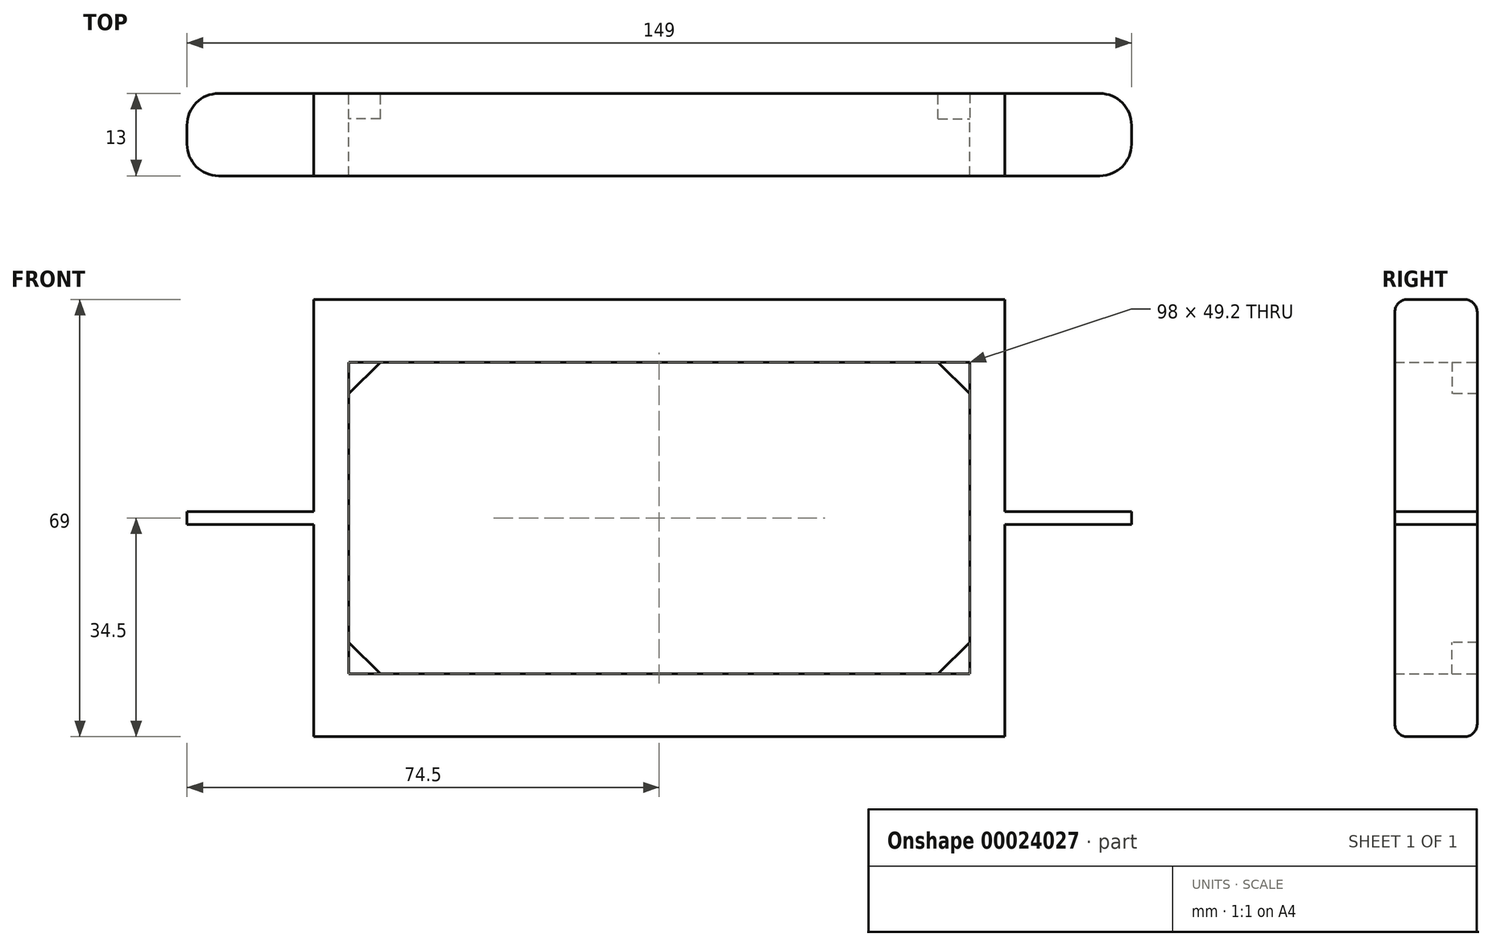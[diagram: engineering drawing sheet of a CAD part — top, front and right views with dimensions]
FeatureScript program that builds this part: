
annotation { "Feature Type Name" : "Feature", "Feature Type Description" : "" }
export const myFeature = defineFeature(function(context is Context, id is Id, definition is map)
    precondition{}
    {
        {
            var Q0;
            Q0=qCreatedBy(makeId("Front.planeOp"),FACE);
            var sketch = newSketch(context, id + "F0", { "sketchPlane" : qUnion([Q0])});
            skLineSegment(sketch, "E0.bottom", {"start": v(-49, -24.6) * mm, "end": v(49, -24.6) * mm});
            skLineSegment(sketch, "E0.top", {"start": v(-49, 24.6) * mm, "end": v(49, 24.6) * mm});
            skLineSegment(sketch, "E0.left", {"start": v(-49, -24.6) * mm, "end": v(-49, 24.6) * mm});
            skLineSegment(sketch, "E0.right", {"start": v(49, -24.6) * mm, "end": v(49, 24.6) * mm});
            skPoint(sketch, "E0.middle", {"position": v(0, 0) * mm});
            skLineSegment(sketch, "E1.bottom", {"start": v(54.5, -34.5) * mm, "end": v(-54.5, -34.5) * mm});
            skLineSegment(sketch, "E1.top", {"start": v(54.5, 34.5) * mm, "end": v(-54.5, 34.5) * mm});
            skLineSegment(sketch, "E1.left", {"start": v(54.5, -34.5) * mm, "end": v(54.5, 34.5) * mm});
            skLineSegment(sketch, "E1.right", {"start": v(-54.5, -34.5) * mm, "end": v(-54.5, 34.5) * mm});
            skLineSegment(sketch, "E2", {"start": v(0, 0) * mm, "end": v(0, -47.06) * mm, "construction": true});
            skLineSegment(sketch, "E3", {"start": v(54.5, 0) * mm, "end": v(74.5, 0) * mm, "construction": true});
            skPoint(sketch, "E3.endSnap0", {"position": v(54.5, 0) * mm});
            skLineSegment(sketch, "E4", {"start": v(74.5, 1) * mm, "end": v(74.5, -1) * mm});
            skLineSegment(sketch, "E5", {"start": v(74.5, -1) * mm, "end": v(54.5, -1) * mm});
            skLineSegment(sketch, "E6", {"start": v(74.5, 1) * mm, "end": v(54.5, 1) * mm});
            skLineSegment(sketch, "E7.MirrorCS", {"start": v(-74.5, -1) * mm, "end": v(-54.5, -1) * mm});
            skLineSegment(sketch, "E8.MirrorCS", {"start": v(-74.5, 1) * mm, "end": v(-54.5, 1) * mm});
            skLineSegment(sketch, "E9.MirrorCS", {"start": v(-74.5, 1) * mm, "end": v(-74.5, -1) * mm});
            skSolve(sketch);
        }
        {
            var Q0;
            Q0=makeQuery(id+"F0.imprint","IMPRINT",FACE,{"disambiguationData":[TD([[makeQuery(id+"F0.imprint","IMPRINT",EDGE,{"derivedFrom":sQuery(id+"F0.wireOp",EDGE,"E0.bottom")}),-1.0]])]});
            var Q1;
            Q1=makeQuery(id+"F0.imprint","IMPRINT",FACE,{"disambiguationData":[TD([[makeQuery(id+"F0.imprint","IMPRINT",EDGE,{"derivedFrom":sQuery(id+"F0.wireOp",EDGE,"E4")}),-1.0]])]});
            var Q2;
            {var subQ0=sQuery(id+"F0.wireOp",EDGE,"E7.MirrorCS");Q2=makeQuery(id+"F0.imprint","IMPRINT",FACE,{"disambiguationData":[TD([[makeQuery(id+"F0.imprint","IMPRINT",EDGE,{"derivedFrom":subQ0}),1.0]])]});}
            extrude(context, id + "F1", {"entities" : qUnion([Q0, Q1, Q2]), "depth" : 13 * mm});
        }
        {
            var Q0;
            Q0=makeQuery(id+"F1.opExtrude","SWEPT_FACE",FACE,{"disambiguationData":[OSD([sQuery(id+"F0.wireOp",EDGE,"E0.left")])]});
            var sketch = newSketch(context, id + "F2", { "sketchPlane" : qUnion([Q0])});
            skLineSegment(sketch, "E10", {"start": v(-6.5, 24.6) * mm, "end": v(-6.5, -24.6) * mm, "construction": true});
            skLineSegment(sketch, "E11", {"start": v(-4, 24.6) * mm, "end": v(-4, 19.6) * mm});
            skLineSegment(sketch, "E12", {"start": v(-4, 19.6) * mm, "end": v(0, 19.6) * mm});
            skLineSegment(sketch, "E13", {"start": v(-6.5, 0) * mm, "end": v(0, 0) * mm, "construction": true});
            skLineSegment(sketch, "E14.MirrorCS", {"start": v(-4, -24.6) * mm, "end": v(-4, -19.6) * mm});
            skLineSegment(sketch, "E15.MirrorCS", {"start": v(-4, -19.6) * mm, "end": v(0, -19.6) * mm});
            skSolve(sketch);
        }
        {
            var Q0;
            Q0=makeQuery(id+"F1.opExtrude","SWEPT_FACE",FACE,{"disambiguationData":[OSD([sQuery(id+"F0.wireOp",EDGE,"E0.right")])]});
            var sketch = newSketch(context, id + "F3", { "sketchPlane" : qUnion([Q0])});
            skLineSegment(sketch, "E16", {"start": v(0, 0) * mm, "end": v(13, 0) * mm, "construction": true});
            skLineSegment(sketch, "E17", {"start": v(6.5, 24.6) * mm, "end": v(6.5, 0) * mm, "construction": true});
            skLineSegment(sketch, "E18.bottom", {"start": v(0, 24.6) * mm, "end": v(4, 24.6) * mm});
            skLineSegment(sketch, "E18.top", {"start": v(0, 19.6) * mm, "end": v(4, 19.6) * mm});
            skLineSegment(sketch, "E18.left", {"start": v(0, 24.6) * mm, "end": v(0, 19.6) * mm});
            skLineSegment(sketch, "E18.right", {"start": v(4, 24.6) * mm, "end": v(4, 19.6) * mm});
            skLineSegment(sketch, "E19.MirrorCS", {"start": v(0, -19.6) * mm, "end": v(4, -19.6) * mm});
            skLineSegment(sketch, "E20.MirrorCS", {"start": v(4, -24.6) * mm, "end": v(4, -19.6) * mm});
            skSolve(sketch);
        }
        {
            var Q0;
            Q0 = qSketchRegion(id + "F2", true);
            var Q1;
            {var subQ0=sQuery(id+"F2.wireOp",EDGE,"E14.MirrorCS");Q1=makeQuery(id+"F2.imprint","IMPRINT",FACE,{"disambiguationData":[TD([[makeQuery(id+"F2.imprint","IMPRINT",EDGE,{"derivedFrom":subQ0}),-1.0]])]});}
            var Q2;
            {var subQ0=sQuery(id+"F2.wireOp",EDGE,"E11");Q2=makeQuery(id+"F2.imprint","IMPRINT",FACE,{"disambiguationData":[TD([[makeQuery(id+"F2.imprint","IMPRINT",EDGE,{"derivedFrom":subQ0}),1.0]])]});}
            extrude(context, id + "F4", {"entities" : qUnion([Q0, Q1, Q2]), "operationType" : NewBodyOperationType.ADD, "depth" : 5 * mm});
        }
        {
            var Q0;
            Q0 = qSketchRegion(id + "F3", true);
            var Q1;
            {var subQ0=sQuery(id+"F3.wireOp",EDGE,"E19.MirrorCS");Q1=makeQuery(id+"F3.imprint","IMPRINT",FACE,{"disambiguationData":[TD([[makeQuery(id+"F3.imprint","IMPRINT",EDGE,{"derivedFrom":subQ0}),-1.0]])]});}
            extrude(context, id + "F5", {"entities" : qUnion([Q0, Q1]), "operationType" : NewBodyOperationType.ADD, "depth" : 5 * mm});
        }
        {
            var Q0;
            Q0=makeQuery(id+"F4.opExtrude","CAP_EDGE",EDGE,{"disambiguationData":[OSD([sQuery(id+"F2.wireOp",EDGE,"E12")])],"isStart":false});
            var Q1;
            Q1=makeQuery(id+"F4.opExtrude","CAP_EDGE",EDGE,{"disambiguationData":[OSD([sQuery(id+"F2.wireOp",EDGE,"E15.MirrorCS")])],"isStart":false});
            var Q2;
            Q2=makeQuery(id+"F5.opExtrude","CAP_EDGE",EDGE,{"disambiguationData":[OSD([sQuery(id+"F3.wireOp",EDGE,"E18.top")])],"isStart":false});
            var Q3;
            Q3=makeQuery(id+"F5.opExtrude","CAP_EDGE",EDGE,{"disambiguationData":[OSD([sQuery(id+"F3.wireOp",EDGE,"E19.MirrorCS")])],"isStart":false});
            chamfer(context, id + "F6", {"entities" : qUnion([Q0, Q1, Q2, Q3]), "width" : 5 * mm, "tangentPropagation" : true});
        }
        {
            var Q0;
            Q0=makeQuery(id+"F1.opExtrude","CAP_EDGE",EDGE,{"disambiguationData":[OSD([sQuery(id+"F0.wireOp",EDGE,"E4")])],"isStart":false});
            var Q1;
            Q1=makeQuery(id+"F1.opExtrude","CAP_EDGE",EDGE,{"disambiguationData":[OSD([sQuery(id+"F0.wireOp",EDGE,"E4")])],"isStart":true});
            var Q2;
            Q2=makeQuery(id+"F1.opExtrude","CAP_EDGE",EDGE,{"disambiguationData":[OSD([sQuery(id+"F0.wireOp",EDGE,"E9.MirrorCS")])],"isStart":true});
            var Q3;
            Q3=makeQuery(id+"F1.opExtrude","CAP_EDGE",EDGE,{"disambiguationData":[OSD([sQuery(id+"F0.wireOp",EDGE,"E9.MirrorCS")])],"isStart":false});
            fillet(context, id + "F7", {"entities" : qUnion([Q0, Q1, Q2, Q3]), "radius" : 5 * mm, "tangentPropagation" : true, "allowEdgeOverflow" : false});
        }
        {
            var Q0;
            Q0=makeQuery(id+"F1.opExtrude","CAP_EDGE",EDGE,{"disambiguationData":[OSD([sQuery(id+"F0.wireOp",EDGE,"E1.bottom")])],"isStart":false});
            var Q1;
            Q1=makeQuery(id+"F1.opExtrude","CAP_EDGE",EDGE,{"disambiguationData":[OSD([sQuery(id+"F0.wireOp",EDGE,"E1.top")])],"isStart":false});
            var Q2;
            Q2=makeQuery(id+"F1.opExtrude","CAP_EDGE",EDGE,{"disambiguationData":[OSD([sQuery(id+"F0.wireOp",EDGE,"E1.bottom")])],"isStart":true});
            var Q3;
            Q3=makeQuery(id+"F1.opExtrude","CAP_EDGE",EDGE,{"disambiguationData":[OSD([sQuery(id+"F0.wireOp",EDGE,"E1.top")])],"isStart":true});
            fillet(context, id + "F8", {"entities" : qUnion([Q0, Q1, Q2, Q3]), "radius" : 2 * mm, "tangentPropagation" : true, "allowEdgeOverflow" : false});
        }
    });
